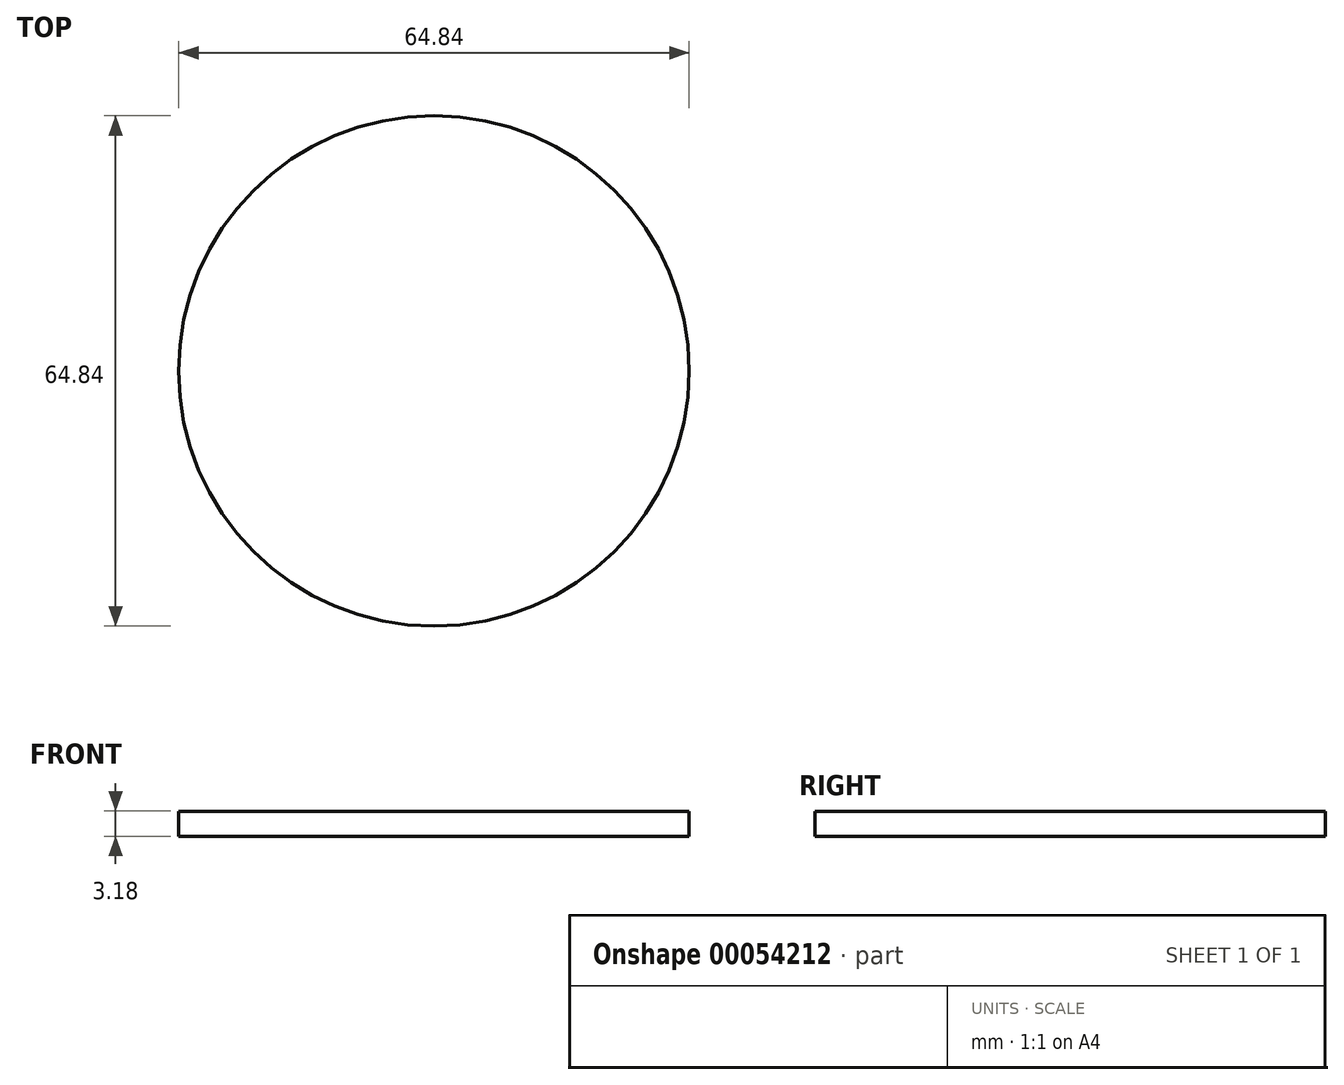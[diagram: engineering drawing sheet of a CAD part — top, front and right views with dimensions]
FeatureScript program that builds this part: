
annotation { "Feature Type Name" : "Feature", "Feature Type Description" : "" }
export const myFeature = defineFeature(function(context is Context, id is Id, definition is map)
    precondition{}
    {
        {
            var Q0;
            Q0=qCreatedBy(makeId("Top.planeOp"),FACE);
            var sketch = newSketch(context, id + "F0", { "sketchPlane" : qUnion([Q0])});
            skCircle(sketch, "E0", {"center": v(0, 0) * mm, "radius": 32.42 * mm});
            skSolve(sketch);
        }
        {
            var Q0;
            Q0=qSketchRegion(id+"F0",true);
            extrude(context, id + "F1", {"entities" : qUnion([Q0]), "depth" : 3.17 * mm});
        }
    });
